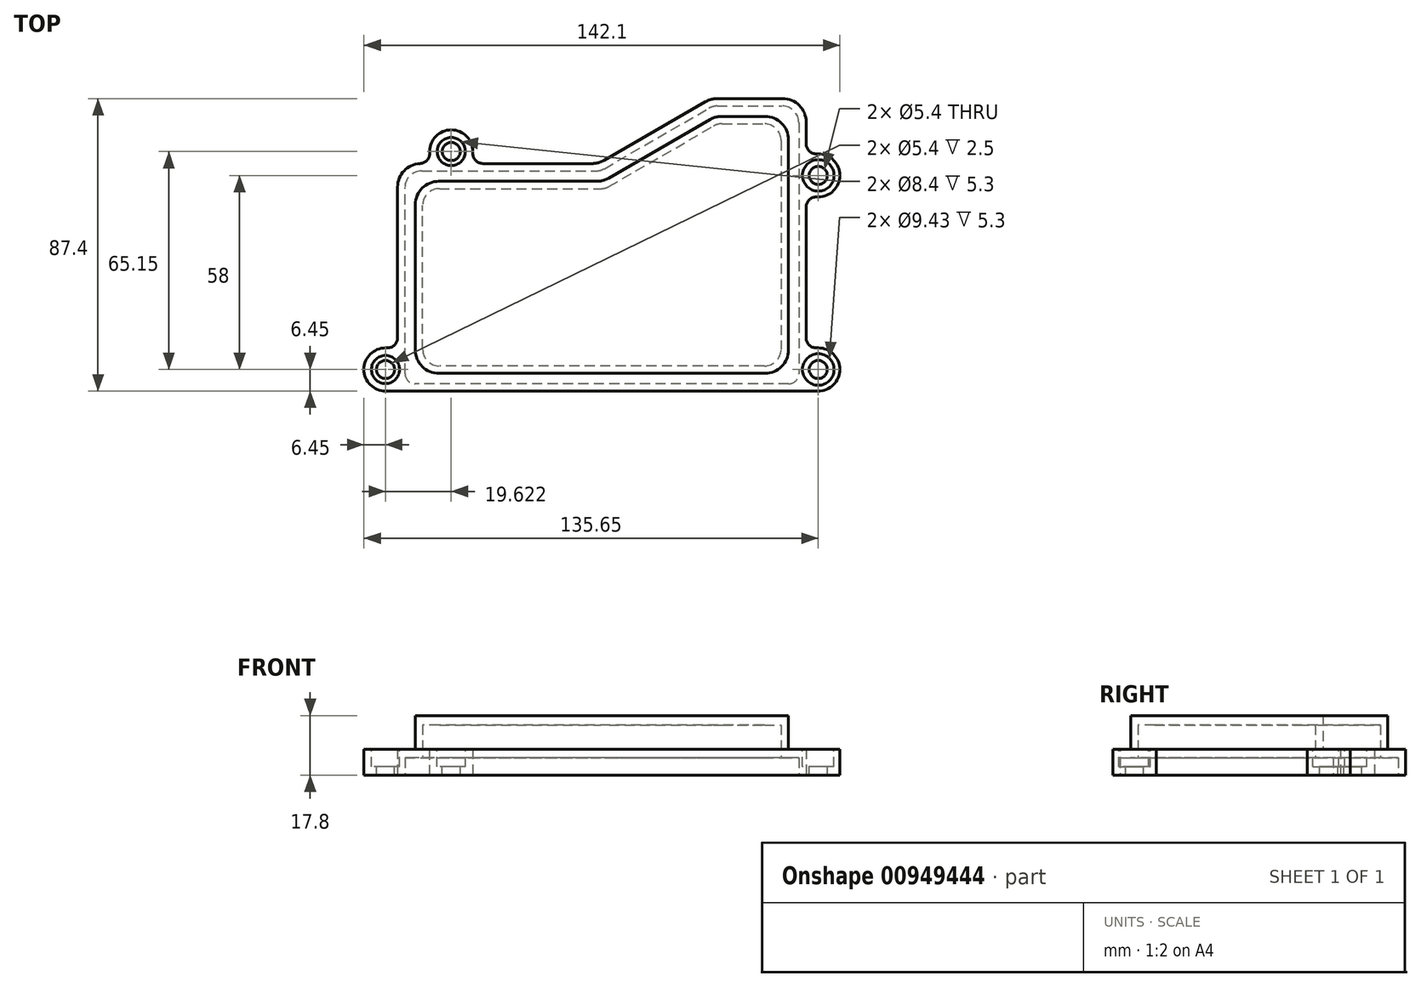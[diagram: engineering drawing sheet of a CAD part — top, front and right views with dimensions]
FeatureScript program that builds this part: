
annotation { "Feature Type Name" : "Feature", "Feature Type Description" : "" }
export const myFeature = defineFeature(function(context is Context, id is Id, definition is map)
    precondition{}
    {
        {
            var Q0;
            Q0=qCreatedBy(makeId("Top.planeOp"),FACE);
            var sketch = newSketch(context, id + "F0", { "sketchPlane" : qUnion([Q0])});
            skLineSegment(sketch, "E0.left", {"start": v(0, 12.9) * mm, "end": v(0, 68) * mm});
            skLineSegment(sketch, "E1", {"start": v(0, 68) * mm, "end": v(9.57, 68) * mm});
            skLineSegment(sketch, "E2", {"start": v(60, 68) * mm, "end": v(93.5, 87.4) * mm});
            skLineSegment(sketch, "E3", {"start": v(93.5, 87.4) * mm, "end": v(122, 87.4) * mm});
            skLineSegment(sketch, "E4", {"start": v(122, 87.4) * mm, "end": v(122, 70.9) * mm});
            skLineSegment(sketch, "E5", {"start": v(122, 0) * mm, "end": v(0, 0) * mm});
            skLineSegment(sketch, "E6.bottom", {"start": v(0, 0) * mm, "end": v(-10.05, 0) * mm});
            skLineSegment(sketch, "E6.top", {"start": v(0, 12.9) * mm, "end": v(-10.05, 12.9) * mm});
            skLineSegment(sketch, "E6.right", {"start": v(-10.05, 0) * mm, "end": v(-10.05, 12.9) * mm});
            skLineSegment(sketch, "E7.bottom", {"start": v(122, 58) * mm, "end": v(132.05, 58) * mm});
            skLineSegment(sketch, "E7.top", {"start": v(122, 70.9) * mm, "end": v(132.05, 70.9) * mm});
            skLineSegment(sketch, "E7.right", {"start": v(132.05, 58) * mm, "end": v(132.05, 70.9) * mm});
            skLineSegment(sketch, "E8.top", {"start": v(9.57, 78.05) * mm, "end": v(22.47, 78.05) * mm});
            skLineSegment(sketch, "E8.left", {"start": v(9.57, 68) * mm, "end": v(9.57, 78.05) * mm});
            skLineSegment(sketch, "E8.right", {"start": v(22.47, 68) * mm, "end": v(22.47, 78.05) * mm});
            skLineSegment(sketch, "E9.trimOffspring", {"start": v(122, 58) * mm, "end": v(122, 12.9) * mm});
            skLineSegment(sketch, "E10.trimOffspring", {"start": v(22.47, 68) * mm, "end": v(60, 68) * mm});
            skLineSegment(sketch, "E11.bottom", {"start": v(122, 0) * mm, "end": v(132.05, 0) * mm});
            skLineSegment(sketch, "E11.top", {"start": v(122, 12.9) * mm, "end": v(132.05, 12.9) * mm});
            skLineSegment(sketch, "E11.right", {"start": v(132.05, 0) * mm, "end": v(132.05, 12.9) * mm});
            skSolve(sketch);
        }
        {
            var Q0;
            Q0 = qSketchRegion(id + "F0", true);
            extrude(context, id + "F1", {"entities" : qUnion([Q0]), "depth" : 7.8 * mm, "offsetDistance" : 25 * mm});
        }
        {
            var Q0;
            Q0=makeQuery(id+"F1.opExtrude","SWEPT_EDGE",EDGE,{"disambiguationData":[OSD([sQuery(id+"F0.wireOp",EDGE,"E6.bottom"),sQuery(id+"F0.wireOp",EDGE,"E6.right")])]});
            var Q1;
            Q1=makeQuery(id+"F1.opExtrude","SWEPT_EDGE",EDGE,{"disambiguationData":[OSD([sQuery(id+"F0.wireOp",EDGE,"E6.top"),sQuery(id+"F0.wireOp",EDGE,"E6.right")])]});
            var Q2;
            Q2=makeQuery(id+"F1.opExtrude","SWEPT_EDGE",EDGE,{"disambiguationData":[OSD([sQuery(id+"F0.wireOp",EDGE,"E8.top"),sQuery(id+"F0.wireOp",EDGE,"E8.left")])]});
            var Q3;
            Q3=makeQuery(id+"F1.opExtrude","SWEPT_EDGE",EDGE,{"disambiguationData":[OSD([sQuery(id+"F0.wireOp",EDGE,"E8.top"),sQuery(id+"F0.wireOp",EDGE,"E8.right")])]});
            var Q4;
            Q4=makeQuery(id+"F1.opExtrude","SWEPT_EDGE",EDGE,{"disambiguationData":[OSD([sQuery(id+"F0.wireOp",EDGE,"E7.top"),sQuery(id+"F0.wireOp",EDGE,"E7.right")])]});
            var Q5;
            Q5=makeQuery(id+"F1.opExtrude","SWEPT_EDGE",EDGE,{"disambiguationData":[OSD([sQuery(id+"F0.wireOp",EDGE,"E7.bottom"),sQuery(id+"F0.wireOp",EDGE,"E7.right")])]});
            var Q6;
            Q6=makeQuery(id+"F1.opExtrude","SWEPT_EDGE",EDGE,{"disambiguationData":[OSD([sQuery(id+"F0.wireOp",EDGE,"E11.top"),sQuery(id+"F0.wireOp",EDGE,"E11.right")])]});
            var Q7;
            Q7=makeQuery(id+"F1.opExtrude","SWEPT_EDGE",EDGE,{"disambiguationData":[OSD([sQuery(id+"F0.wireOp",EDGE,"E11.bottom"),sQuery(id+"F0.wireOp",EDGE,"E11.right")])]});
            fillet(context, id + "F2", {"entities" : qUnion([Q0, Q1, Q2, Q3, Q4, Q5, Q6, Q7]), "radius" : (12.9 / 2) * mm, "tangentPropagation" : true, "allowEdgeOverflow" : false});
        }
        {
            var Q0;
            Q0=makeQuery(id+"F1.opExtrude","CAP_FACE",FACE,{"disambiguationData":[OSD([sQuery(id+"F0.wireOp",EDGE,"E0.left"),sQuery(id+"F0.wireOp",EDGE,"E1"),sQuery(id+"F0.wireOp",EDGE,"E2"),sQuery(id+"F0.wireOp",EDGE,"E3"),sQuery(id+"F0.wireOp",EDGE,"E4"),sQuery(id+"F0.wireOp",EDGE,"E5"),sQuery(id+"F0.wireOp",EDGE,"E6.bottom"),sQuery(id+"F0.wireOp",EDGE,"E6.top"),sQuery(id+"F0.wireOp",EDGE,"E6.right"),sQuery(id+"F0.wireOp",EDGE,"E7.bottom"),sQuery(id+"F0.wireOp",EDGE,"E7.top"),sQuery(id+"F0.wireOp",EDGE,"E7.right"),sQuery(id+"F0.wireOp",EDGE,"E8.top"),sQuery(id+"F0.wireOp",EDGE,"E8.left"),sQuery(id+"F0.wireOp",EDGE,"E8.right"),sQuery(id+"F0.wireOp",EDGE,"E9.trimOffspring"),sQuery(id+"F0.wireOp",EDGE,"E10.trimOffspring"),sQuery(id+"F0.wireOp",EDGE,"E11.bottom"),sQuery(id+"F0.wireOp",EDGE,"E11.top"),sQuery(id+"F0.wireOp",EDGE,"E11.right")])],"isStart":false});
            var sketch = newSketch(context, id + "F3", { "sketchPlane" : qUnion([Q0])});
            skCircle(sketch, "E12", {"center": v(-3.6, 6.45) * mm, "radius": 2.7 * mm});
            skCircle(sketch, "E13", {"center": v(16.02, 71.6) * mm, "radius": 2.7 * mm});
            skCircle(sketch, "E14", {"center": v(125.6, 64.45) * mm, "radius": 2.7 * mm});
            skCircle(sketch, "E15", {"center": v(125.6, 6.45) * mm, "radius": 2.7 * mm});
            skSolve(sketch);
        }
        {
            var Q0;
            Q0 = qSketchRegion(id + "F3", true);
            extrude(context, id + "F4", {"entities" : qUnion([Q0]), "operationType" : NewBodyOperationType.REMOVE, "endBound" : BoundingType.THROUGH_ALL, "oppositeDirection" : true, "depth" : 25 * mm, "offsetDistance" : 25 * mm});
        }
        {
            var Q0;
            Q0=makeQuery(id+"F1.opExtrude","CAP_FACE",FACE,{"disambiguationData":[OSD([sQuery(id+"F0.wireOp",EDGE,"E0.left"),sQuery(id+"F0.wireOp",EDGE,"E1"),sQuery(id+"F0.wireOp",EDGE,"E2"),sQuery(id+"F0.wireOp",EDGE,"E3"),sQuery(id+"F0.wireOp",EDGE,"E4"),sQuery(id+"F0.wireOp",EDGE,"E5"),sQuery(id+"F0.wireOp",EDGE,"E6.bottom"),sQuery(id+"F0.wireOp",EDGE,"E6.top"),sQuery(id+"F0.wireOp",EDGE,"E6.right"),sQuery(id+"F0.wireOp",EDGE,"E7.bottom"),sQuery(id+"F0.wireOp",EDGE,"E7.top"),sQuery(id+"F0.wireOp",EDGE,"E7.right"),sQuery(id+"F0.wireOp",EDGE,"E8.top"),sQuery(id+"F0.wireOp",EDGE,"E8.left"),sQuery(id+"F0.wireOp",EDGE,"E8.right"),sQuery(id+"F0.wireOp",EDGE,"E9.trimOffspring"),sQuery(id+"F0.wireOp",EDGE,"E10.trimOffspring"),sQuery(id+"F0.wireOp",EDGE,"E11.bottom"),sQuery(id+"F0.wireOp",EDGE,"E11.top"),sQuery(id+"F0.wireOp",EDGE,"E11.right")])],"isStart":false});
            var sketch = newSketch(context, id + "F5", { "sketchPlane" : qUnion([Q0])});
            skCircle(sketch, "E16", {"center": v(-3.6, 6.45) * mm, "radius": 4.2 * mm});
            skCircle(sketch, "E17", {"center": v(16.02, 71.6) * mm, "radius": 4.2 * mm});
            skCircle(sketch, "E18", {"center": v(125.6, 64.45) * mm, "radius": 4.72 * mm});
            skCircle(sketch, "E19", {"center": v(125.6, 6.45) * mm, "radius": 4.72 * mm});
            skSolve(sketch);
        }
        {
            var Q0;
            Q0 = qSketchRegion(id + "F5", true);
            extrude(context, id + "F6", {"entities" : qUnion([Q0]), "operationType" : NewBodyOperationType.REMOVE, "oppositeDirection" : true, "depth" : 5.3 * mm, "offsetDistance" : 25 * mm});
        }
        {
            var Q0;
            Q0=makeQuery(id+"F1.opExtrude","CAP_FACE",FACE,{"disambiguationData":[OSD([sQuery(id+"F0.wireOp",EDGE,"E0.left"),sQuery(id+"F0.wireOp",EDGE,"E1"),sQuery(id+"F0.wireOp",EDGE,"E2"),sQuery(id+"F0.wireOp",EDGE,"E3"),sQuery(id+"F0.wireOp",EDGE,"E4"),sQuery(id+"F0.wireOp",EDGE,"E5"),sQuery(id+"F0.wireOp",EDGE,"E6.bottom"),sQuery(id+"F0.wireOp",EDGE,"E6.top"),sQuery(id+"F0.wireOp",EDGE,"E6.right"),sQuery(id+"F0.wireOp",EDGE,"E7.bottom"),sQuery(id+"F0.wireOp",EDGE,"E7.top"),sQuery(id+"F0.wireOp",EDGE,"E7.right"),sQuery(id+"F0.wireOp",EDGE,"E8.top"),sQuery(id+"F0.wireOp",EDGE,"E8.left"),sQuery(id+"F0.wireOp",EDGE,"E8.right"),sQuery(id+"F0.wireOp",EDGE,"E9.trimOffspring"),sQuery(id+"F0.wireOp",EDGE,"E10.trimOffspring"),sQuery(id+"F0.wireOp",EDGE,"E11.bottom"),sQuery(id+"F0.wireOp",EDGE,"E11.top"),sQuery(id+"F0.wireOp",EDGE,"E11.right")])],"isStart":false});
            var sketch = newSketch(context, id + "F7", { "sketchPlane" : qUnion([Q0])});
            skLineSegment(sketch, "E20", {"start": v(0, 68) * mm, "end": v(60, 68) * mm});
            skLineSegment(sketch, "E21", {"start": v(60, 68) * mm, "end": v(93.5, 87.4) * mm});
            skLineSegment(sketch, "E22", {"start": v(93.5, 87.4) * mm, "end": v(122, 87.4) * mm});
            skLineSegment(sketch, "E23", {"start": v(122, 87.4) * mm, "end": v(122, 0) * mm});
            skLineSegment(sketch, "E24", {"start": v(122, 0) * mm, "end": v(0, 0) * mm});
            skLineSegment(sketch, "E25", {"start": v(0, 0) * mm, "end": v(0, 68) * mm});
            skLineSegment(sketch, "E26.0", {"start": v(5.3, 5.3) * mm, "end": v(5.3, 62.7) * mm});
            skLineSegment(sketch, "E26.1", {"start": v(61.42, 62.7) * mm, "end": v(94.92, 82.1) * mm});
            skLineSegment(sketch, "E26.2", {"start": v(94.92, 82.1) * mm, "end": v(116.7, 82.1) * mm});
            skLineSegment(sketch, "E26.3", {"start": v(5.3, 62.7) * mm, "end": v(61.42, 62.7) * mm});
            skLineSegment(sketch, "E26.4", {"start": v(116.7, 82.1) * mm, "end": v(116.7, 5.3) * mm});
            skLineSegment(sketch, "E26.5", {"start": v(116.7, 5.3) * mm, "end": v(5.3, 5.3) * mm});
            skSolve(sketch);
        }
        {
            var Q0;
            Q0=makeQuery(id+"F7.imprint","IMPRINT",FACE,{"disambiguationData":[TD([[makeQuery(id+"F7.imprint","IMPRINT",EDGE,{"derivedFrom":sQuery(id+"F7.wireOp",EDGE,"E26.0")}),-1.0]])]});
            extrude(context, id + "F8", {"entities" : qUnion([Q0]), "operationType" : NewBodyOperationType.ADD, "depth" : 10 * mm, "offsetDistance" : 25 * mm});
        }
        {
            var Q0;
            Q0=makeQuery(id+"F1.opExtrude","CAP_FACE",FACE,{"disambiguationData":[OSD([sQuery(id+"F0.wireOp",EDGE,"E0.left"),sQuery(id+"F0.wireOp",EDGE,"E1"),sQuery(id+"F0.wireOp",EDGE,"E2"),sQuery(id+"F0.wireOp",EDGE,"E3"),sQuery(id+"F0.wireOp",EDGE,"E4"),sQuery(id+"F0.wireOp",EDGE,"E5"),sQuery(id+"F0.wireOp",EDGE,"E6.bottom"),sQuery(id+"F0.wireOp",EDGE,"E6.top"),sQuery(id+"F0.wireOp",EDGE,"E6.right"),sQuery(id+"F0.wireOp",EDGE,"E7.bottom"),sQuery(id+"F0.wireOp",EDGE,"E7.top"),sQuery(id+"F0.wireOp",EDGE,"E7.right"),sQuery(id+"F0.wireOp",EDGE,"E8.top"),sQuery(id+"F0.wireOp",EDGE,"E8.left"),sQuery(id+"F0.wireOp",EDGE,"E8.right"),sQuery(id+"F0.wireOp",EDGE,"E9.trimOffspring"),sQuery(id+"F0.wireOp",EDGE,"E10.trimOffspring"),sQuery(id+"F0.wireOp",EDGE,"E11.bottom"),sQuery(id+"F0.wireOp",EDGE,"E11.top"),sQuery(id+"F0.wireOp",EDGE,"E11.right")])],"isStart":true});
            var sketch = newSketch(context, id + "F9", { "sketchPlane" : qUnion([Q0])});
            skLineSegment(sketch, "E27", {"start": v(0, 0) * mm, "end": v(0, -68) * mm});
            skLineSegment(sketch, "E28", {"start": v(0, -68) * mm, "end": v(60, -68) * mm});
            skLineSegment(sketch, "E29", {"start": v(60, -68) * mm, "end": v(93.5, -87.4) * mm});
            skLineSegment(sketch, "E30", {"start": v(93.5, -87.4) * mm, "end": v(122, -87.4) * mm});
            skLineSegment(sketch, "E31", {"start": v(122, -87.4) * mm, "end": v(122, 0) * mm});
            skLineSegment(sketch, "E32", {"start": v(122, 0) * mm, "end": v(0, 0) * mm});
            skLineSegment(sketch, "E33.0", {"start": v(119.8, -85.2) * mm, "end": v(119.8, -2.2) * mm});
            skLineSegment(sketch, "E33.1", {"start": v(2.2, -2.2) * mm, "end": v(2.2, -65.8) * mm});
            skLineSegment(sketch, "E33.2", {"start": v(2.2, -65.8) * mm, "end": v(60.6, -65.8) * mm});
            skLineSegment(sketch, "E33.3", {"start": v(119.8, -2.2) * mm, "end": v(2.2, -2.2) * mm});
            skLineSegment(sketch, "E33.4", {"start": v(60.6, -65.8) * mm, "end": v(94.1, -85.2) * mm});
            skLineSegment(sketch, "E33.5", {"start": v(94.1, -85.2) * mm, "end": v(119.8, -85.2) * mm});
            skSolve(sketch);
        }
        {
            var Q0;
            Q0=makeQuery(id+"F9.imprint","IMPRINT",FACE,{"disambiguationData":[TD([[makeQuery(id+"F9.imprint","IMPRINT",EDGE,{"derivedFrom":sQuery(id+"F9.wireOp",EDGE,"E33.0")}),1.0]])]});
            extrude(context, id + "F10", {"entities" : qUnion([Q0]), "operationType" : NewBodyOperationType.REMOVE, "oppositeDirection" : true, "depth" : 5.2 * mm, "offsetDistance" : 25 * mm});
        }
        {
            var Q0;
            Q0=makeQuery(id+"F10.boolean.opBoolean","COPY",FACE,{"derivedFrom":makeQuery(id+"F10.opExtrude","CAP_FACE",FACE,{"disambiguationData":[OSD([sQuery(id+"F9.wireOp",EDGE,"E33.0"),sQuery(id+"F9.wireOp",EDGE,"E33.1"),sQuery(id+"F9.wireOp",EDGE,"E33.2"),sQuery(id+"F9.wireOp",EDGE,"E33.3"),sQuery(id+"F9.wireOp",EDGE,"E33.4"),sQuery(id+"F9.wireOp",EDGE,"E33.5")])],"isStart":false})});
            var sketch = newSketch(context, id + "F11", { "sketchPlane" : qUnion([Q0])});
            skLineSegment(sketch, "E34.0", {"start": v(7.5, -7.5) * mm, "end": v(7.5, -60.5) * mm});
            skLineSegment(sketch, "E34.1", {"start": v(62.01, -60.5) * mm, "end": v(95.51, -79.9) * mm});
            skLineSegment(sketch, "E34.2", {"start": v(95.51, -79.9) * mm, "end": v(114.5, -79.9) * mm});
            skLineSegment(sketch, "E34.3", {"start": v(7.5, -60.5) * mm, "end": v(62.01, -60.5) * mm});
            skLineSegment(sketch, "E34.4", {"start": v(114.5, -79.9) * mm, "end": v(114.5, -7.5) * mm});
            skLineSegment(sketch, "E34.5", {"start": v(114.5, -7.5) * mm, "end": v(7.5, -7.5) * mm});
            skSolve(sketch);
        }
        {
            var Q0;
            Q0=makeQuery(id+"F11.imprint","IMPRINT",FACE,{"disambiguationData":[TD([[makeQuery(id+"F11.imprint","IMPRINT",EDGE,{"derivedFrom":sQuery(id+"F11.wireOp",EDGE,"E34.0")}),1.0]])]});
            extrude(context, id + "F12", {"entities" : qUnion([Q0]), "operationType" : NewBodyOperationType.REMOVE, "oppositeDirection" : true, "depth" : 9.8 * mm, "offsetDistance" : 25 * mm});
        }
        {
            var Q0;
            Q0=makeQuery(id+"F12.boolean.opBoolean","COPY",EDGE,{"derivedFrom":makeQuery(id+"F12.opExtrude","SWEPT_EDGE",EDGE,{"disambiguationData":[OSD([sQuery(id+"F11.wireOp",EDGE,"E34.2"),sQuery(id+"F11.wireOp",EDGE,"E34.4")])]})});
            var Q1;
            Q1=makeQuery(id+"F10.boolean.opBoolean","COPY",EDGE,{"derivedFrom":makeQuery(id+"F10.opExtrude","SWEPT_EDGE",EDGE,{"disambiguationData":[OSD([sQuery(id+"F9.wireOp",EDGE,"E33.0"),sQuery(id+"F9.wireOp",EDGE,"E33.5")])]})});
            var Q2;
            Q2=makeQuery(id+"F12.boolean.opBoolean","COPY",EDGE,{"derivedFrom":makeQuery(id+"F12.opExtrude","SWEPT_EDGE",EDGE,{"disambiguationData":[OSD([sQuery(id+"F11.wireOp",EDGE,"E34.0"),sQuery(id+"F11.wireOp",EDGE,"E34.3")])]})});
            var Q3;
            Q3=makeQuery(id+"F10.boolean.opBoolean","COPY",EDGE,{"derivedFrom":makeQuery(id+"F10.opExtrude","SWEPT_EDGE",EDGE,{"disambiguationData":[OSD([sQuery(id+"F9.wireOp",EDGE,"E33.1"),sQuery(id+"F9.wireOp",EDGE,"E33.2")])]})});
            var Q4;
            Q4=makeQuery(id+"F12.boolean.opBoolean","COPY",EDGE,{"derivedFrom":makeQuery(id+"F12.opExtrude","SWEPT_EDGE",EDGE,{"disambiguationData":[OSD([sQuery(id+"F11.wireOp",EDGE,"E34.4"),sQuery(id+"F11.wireOp",EDGE,"E34.5")])]})});
            var Q5;
            Q5=makeQuery(id+"F12.boolean.opBoolean","COPY",EDGE,{"derivedFrom":makeQuery(id+"F12.opExtrude","SWEPT_EDGE",EDGE,{"disambiguationData":[OSD([sQuery(id+"F11.wireOp",EDGE,"E34.0"),sQuery(id+"F11.wireOp",EDGE,"E34.5")])]})});
            var Q6;
            Q6=makeQuery(id+"F12.boolean.opBoolean","COPY",EDGE,{"derivedFrom":makeQuery(id+"F12.opExtrude","SWEPT_EDGE",EDGE,{"disambiguationData":[OSD([sQuery(id+"F11.wireOp",EDGE,"E34.1"),sQuery(id+"F11.wireOp",EDGE,"E34.2")])]})});
            var Q7;
            Q7=makeQuery(id+"F12.boolean.opBoolean","COPY",EDGE,{"derivedFrom":makeQuery(id+"F12.opExtrude","SWEPT_EDGE",EDGE,{"disambiguationData":[OSD([sQuery(id+"F11.wireOp",EDGE,"E34.1"),sQuery(id+"F11.wireOp",EDGE,"E34.3")])]})});
            var Q8;
            Q8=makeQuery(id+"F10.boolean.opBoolean","COPY",EDGE,{"derivedFrom":makeQuery(id+"F10.opExtrude","SWEPT_EDGE",EDGE,{"disambiguationData":[OSD([sQuery(id+"F9.wireOp",EDGE,"E33.2"),sQuery(id+"F9.wireOp",EDGE,"E33.4")])]})});
            var Q9;
            Q9=makeQuery(id+"F10.boolean.opBoolean","COPY",EDGE,{"derivedFrom":makeQuery(id+"F10.opExtrude","SWEPT_EDGE",EDGE,{"disambiguationData":[OSD([sQuery(id+"F9.wireOp",EDGE,"E33.4"),sQuery(id+"F9.wireOp",EDGE,"E33.5")])]})});
            fillet(context, id + "F13", {"entities" : qUnion([Q0, Q1, Q2, Q3, Q4, Q5, Q6, Q7, Q8, Q9]), "radius" : 5 * mm, "tangentPropagation" : true, "allowEdgeOverflow" : false});
        }
        {
            var Q0;
            Q0=makeQuery(id+"F1.opExtrude","SWEPT_EDGE",EDGE,{"disambiguationData":[OSD([sQuery(id+"F0.wireOp",EDGE,"E3"),sQuery(id+"F0.wireOp",EDGE,"E4")])]});
            var Q1;
            Q1=makeQuery(id+"F1.opExtrude","SWEPT_EDGE",EDGE,{"disambiguationData":[OSD([sQuery(id+"F0.wireOp",EDGE,"E2"),sQuery(id+"F0.wireOp",EDGE,"E3")])]});
            var Q2;
            Q2=makeQuery(id+"F1.opExtrude","SWEPT_EDGE",EDGE,{"disambiguationData":[OSD([sQuery(id+"F0.wireOp",EDGE,"E2"),sQuery(id+"F0.wireOp",EDGE,"E10.trimOffspring")])]});
            var Q3;
            Q3=makeQuery(id+"F8.opExtrude","SWEPT_EDGE",EDGE,{"disambiguationData":[OSD([sQuery(id+"F7.wireOp",EDGE,"E26.1"),sQuery(id+"F7.wireOp",EDGE,"E26.3")])]});
            var Q4;
            Q4=makeQuery(id+"F8.opExtrude","SWEPT_EDGE",EDGE,{"disambiguationData":[OSD([sQuery(id+"F7.wireOp",EDGE,"E26.1"),sQuery(id+"F7.wireOp",EDGE,"E26.2")])]});
            var Q5;
            Q5=makeQuery(id+"F8.opExtrude","SWEPT_EDGE",EDGE,{"disambiguationData":[OSD([sQuery(id+"F7.wireOp",EDGE,"E26.2"),sQuery(id+"F7.wireOp",EDGE,"E26.4")])]});
            var Q6;
            Q6=makeQuery(id+"F8.opExtrude","SWEPT_EDGE",EDGE,{"disambiguationData":[OSD([sQuery(id+"F7.wireOp",EDGE,"E26.4"),sQuery(id+"F7.wireOp",EDGE,"E26.5")])]});
            var Q7;
            Q7=makeQuery(id+"F8.opExtrude","SWEPT_EDGE",EDGE,{"disambiguationData":[OSD([sQuery(id+"F7.wireOp",EDGE,"E26.0"),sQuery(id+"F7.wireOp",EDGE,"E26.5")])]});
            var Q8;
            Q8=makeQuery(id+"F8.opExtrude","SWEPT_EDGE",EDGE,{"disambiguationData":[OSD([sQuery(id+"F7.wireOp",EDGE,"E26.0"),sQuery(id+"F7.wireOp",EDGE,"E26.3")])]});
            var Q9;
            Q9=makeQuery(id+"F1.opExtrude","SWEPT_EDGE",EDGE,{"disambiguationData":[OSD([sQuery(id+"F0.wireOp",EDGE,"E0.left"),sQuery(id+"F0.wireOp",EDGE,"E1")])]});
            fillet(context, id + "F14", {"entities" : qUnion([Q0, Q1, Q2, Q3, Q4, Q5, Q6, Q7, Q8, Q9]), "radius" : 7 * mm, "tangentPropagation" : true, "allowEdgeOverflow" : false});
        }
        {
            var Q0;
            Q0=makeQuery(id+"F10.boolean.opBoolean","COPY",EDGE,{"derivedFrom":makeQuery(id+"F10.opExtrude","SWEPT_EDGE",EDGE,{"disambiguationData":[OSD([sQuery(id+"F9.wireOp",EDGE,"E33.0"),sQuery(id+"F9.wireOp",EDGE,"E33.3")])]})});
            var Q1;
            Q1=makeQuery(id+"F10.boolean.opBoolean","COPY",EDGE,{"derivedFrom":makeQuery(id+"F10.opExtrude","SWEPT_EDGE",EDGE,{"disambiguationData":[OSD([sQuery(id+"F9.wireOp",EDGE,"E33.1"),sQuery(id+"F9.wireOp",EDGE,"E33.3")])]})});
            fillet(context, id + "F15", {"entities" : qUnion([Q0, Q1]), "radius" : 3 * mm, "tangentPropagation" : true, "allowEdgeOverflow" : false});
        }
        {
            var Q0;
            Q0=makeQuery(id+"F1.opExtrude","SWEPT_EDGE",EDGE,{"disambiguationData":[OSD([sQuery(id+"F0.wireOp",EDGE,"E0.left"),sQuery(id+"F0.wireOp",EDGE,"E6.top")])]});
            var Q1;
            Q1=makeQuery(id+"F1.opExtrude","SWEPT_EDGE",EDGE,{"disambiguationData":[OSD([sQuery(id+"F0.wireOp",EDGE,"E1"),sQuery(id+"F0.wireOp",EDGE,"E8.left")])]});
            var Q2;
            Q2=makeQuery(id+"F1.opExtrude","SWEPT_EDGE",EDGE,{"disambiguationData":[OSD([sQuery(id+"F0.wireOp",EDGE,"E8.right"),sQuery(id+"F0.wireOp",EDGE,"E10.trimOffspring")])]});
            var Q3;
            Q3=makeQuery(id+"F1.opExtrude","SWEPT_EDGE",EDGE,{"disambiguationData":[OSD([sQuery(id+"F0.wireOp",EDGE,"E4"),sQuery(id+"F0.wireOp",EDGE,"E7.top")])]});
            var Q4;
            Q4=makeQuery(id+"F1.opExtrude","SWEPT_EDGE",EDGE,{"disambiguationData":[OSD([sQuery(id+"F0.wireOp",EDGE,"E7.bottom"),sQuery(id+"F0.wireOp",EDGE,"E9.trimOffspring")])]});
            var Q5;
            Q5=makeQuery(id+"F1.opExtrude","SWEPT_EDGE",EDGE,{"disambiguationData":[OSD([sQuery(id+"F0.wireOp",EDGE,"E9.trimOffspring"),sQuery(id+"F0.wireOp",EDGE,"E11.top")])]});
            fillet(context, id + "F16", {"entities" : qUnion([Q0, Q1, Q2, Q3, Q4, Q5]), "radius" : 3 * mm, "tangentPropagation" : true, "allowEdgeOverflow" : false});
        }
    });
